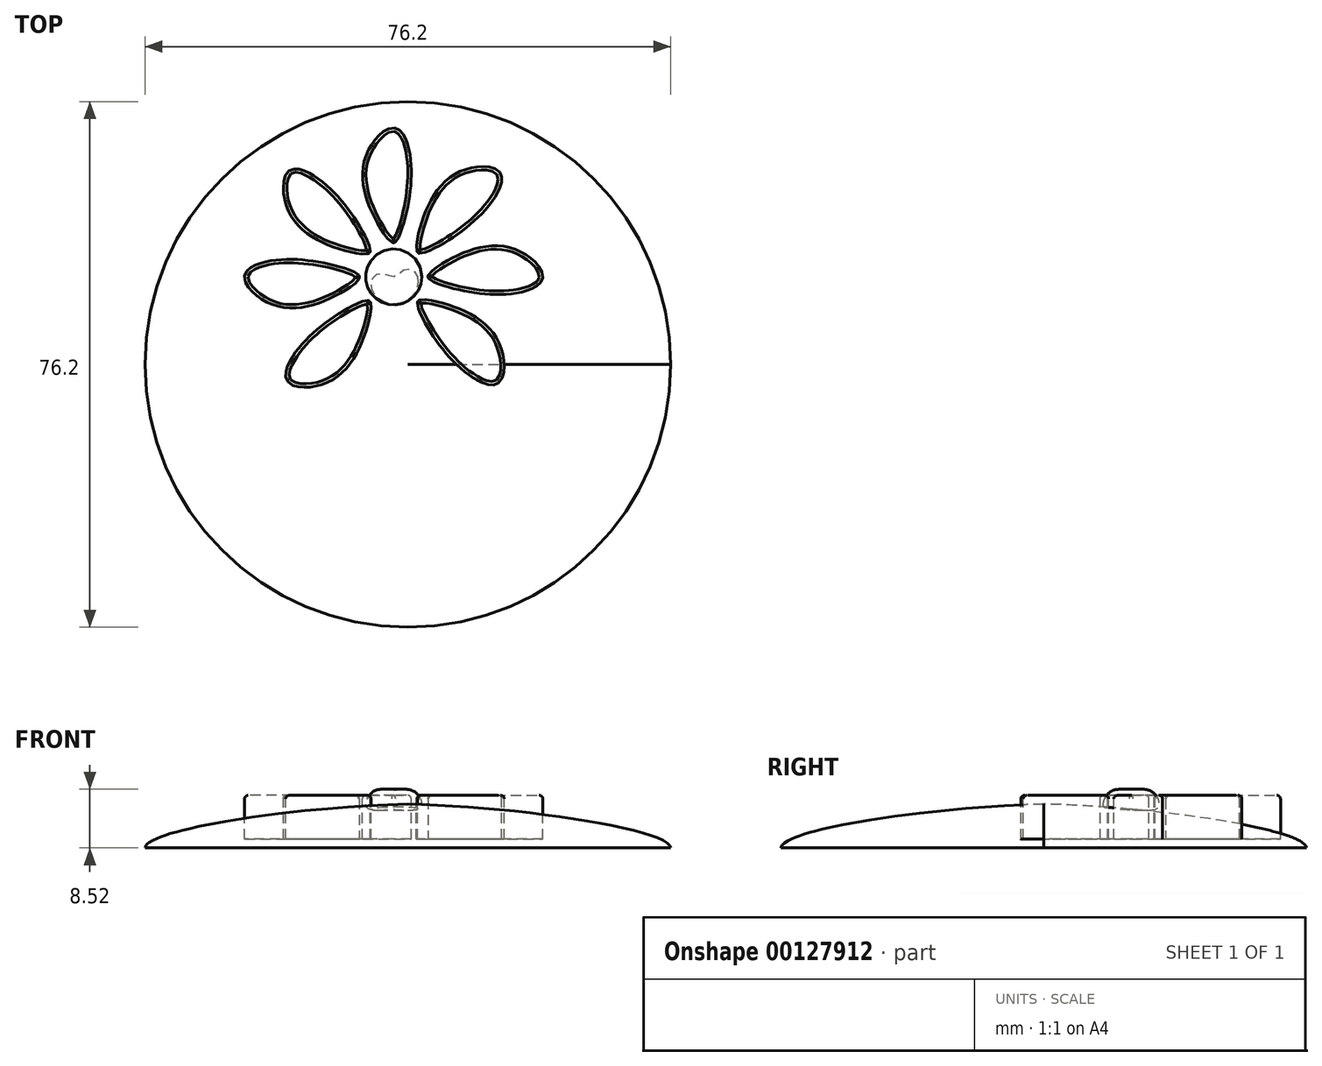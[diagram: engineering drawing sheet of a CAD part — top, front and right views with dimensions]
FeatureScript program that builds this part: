
annotation { "Feature Type Name" : "Feature", "Feature Type Description" : "" }
export const myFeature = defineFeature(function(context is Context, id is Id, definition is map)
    precondition{}
    {
        {
            var Q0;
            Q0=qCreatedBy(makeId("Front.planeOp"),FACE);
            var sketch = newSketch(context, id + "F0", { "sketchPlane" : qUnion([Q0])});
            skLineSegment(sketch, "E0", {"start": v(0, 0) * mm, "end": v(0, 6.35) * mm});
            skLineSegment(sketch, "E1", {"start": v(0, 0) * mm, "end": v(38.1, 0) * mm});
            skFitSpline(sketch, "E2", {"points": [v(0, 6.35) * mm, v(38.1, 0) * mm], "startDerivative": vector(47.97, -0.98) * mm, "endDerivative": vector(0.25, -8.22) * mm});
            skSolve(sketch);
        }
        {
            var Q0;
            Q0 = qSketchRegion(id + "F0", true);
            var Q1;
            Q1=sQuery(id+"F0.wireOp",EDGE,"E0");
            revolve(context, id + "F1", {"entities" : qUnion([Q0]), "axis" : qUnion([Q1]), "revolveType" : RevolveType.FULL});
        }
        {
            var Q0;
            Q0=qCreatedBy(makeId("Front.planeOp"),FACE);
            cPlane(context, id + "F2", {"entities" : qUnion([Q0]), "cplaneType" : CPlaneType.OFFSET, "offset" : 12.7 * mm, "oppositeDirection" : true, "width" : 152.4 * mm, "height" : 152.4 * mm});
        }
        {
            var Q0;
            Q0=qCreatedBy(id+"F2.planeOp",FACE);
            var sketch = newSketch(context, id + "F3", { "sketchPlane" : qUnion([Q0])});
            skFitSpline(sketch, "E3", {"points": [v(-2.05, 8.38) * mm, v(1.14, 8.02) * mm, v(1.9, 5.93) * mm, v(-2.05, 5.58) * mm], "startDerivative": vector(11.75, 1.57) * mm, "endDerivative": vector(-13.9, 0.27) * mm});
            skLineSegment(sketch, "E4", {"start": v(-2.05, 8.38) * mm, "end": v(-2.05, 5.58) * mm});
            skSolve(sketch);
        }
        {
            var Q0;
            Q0 = qSketchRegion(id + "F3", true);
            var Q1;
            Q1=sQuery(id+"F3.wireOp",EDGE,"E4");
            revolve(context, id + "F4", {"operationType" : NewBodyOperationType.ADD, "entities" : qUnion([Q0]), "axis" : qUnion([Q1]), "revolveType" : RevolveType.FULL});
        }
        {
            var Q0;
            Q0=qCreatedBy(makeId("Top.planeOp"),FACE);
            cPlane(context, id + "F5", {"entities" : qUnion([Q0]), "cplaneType" : CPlaneType.OFFSET, "offset" : 7.62 * mm, "width" : 152.4 * mm, "height" : 152.4 * mm});
        }
        {
            var Q0;
            Q0=qCreatedBy(id+"F5.planeOp",FACE);
            var sketch = newSketch(context, id + "F6", { "sketchPlane" : qUnion([Q0])});
            skFitSpline(sketch, "E5", {"points": [v(2.92, 12.74) * mm, v(4.8, 14.51) * mm, v(14.25, 17.09) * mm, v(19.56, 12.58) * mm, v(13.6, 10.16) * mm, v(4.2, 11.77) * mm, v(2.92, 12.74) * mm]});
            skSolve(sketch);
        }
        {
            var Q0;
            Q0 = qSketchRegion(id + "F6", true);
            extrude(context, id + "F7", {"entities" : qUnion([Q0]), "oppositeDirection" : true, "depth" : 6.35 * mm});
        }
        {
            var Q0;
            Q0=makeQuery(id+"F7.opExtrude","CAP_EDGE",EDGE,{"disambiguationData":[OSD([sQuery(id+"F6.wireOp",EDGE,"E5")])],"isStart":true});
            fillet(context, id + "F8", {"entities" : qUnion([Q0]), "radius" : 0.5 * mm, "tangentPropagation" : true, "allowEdgeOverflow" : false});
        }
        {
            var Q0;
            Q0=makeQuery(id+"F7.opExtrude","SWEPT_BODY",BODY,{"disambiguationData":[OSD([sQuery(id+"F6.wireOp",EDGE,"E5")])]});
            var Q1;
            Q1=sQuery(id+"F3.wireOp",EDGE,"E4");
            circularPattern(context, id + "F9", {"entities" : qUnion([Q0]), "axis" : qUnion([Q1]), "angle" : 360 * degree, "instanceCount" : 8, "equalSpace" : true});
        }
        {
            var Q0;
            Q0=makeQuery(id+"F9.opPattern","COPY",BODY,{"derivedFrom":makeQuery(id+"F7.opExtrude","SWEPT_BODY",BODY,{"disambiguationData":[OSD([sQuery(id+"F6.wireOp",EDGE,"E5")])]}),"instanceName":"2"});
            deleteBodies(context, id + "F10", {"entities" : qUnion([Q0])});
        }
        {
            var Q0;
            Q0=qCreatedBy(id+"F5.planeOp",FACE);
            var sketch = newSketch(context, id + "F11", { "sketchPlane" : qUnion([Q0])});
            skFitSpline(sketch, "E6", {"points": [v(-1.9, 9.4) * mm, v(0, -2.84) * mm, v(-3.81, -12.6) * mm, v(2.5, -26.75) * mm], "startDerivative": vector(12.67, -38.94) * mm, "endDerivative": vector(27.05, -40.6) * mm});
            skSolve(sketch);
        }
    });
